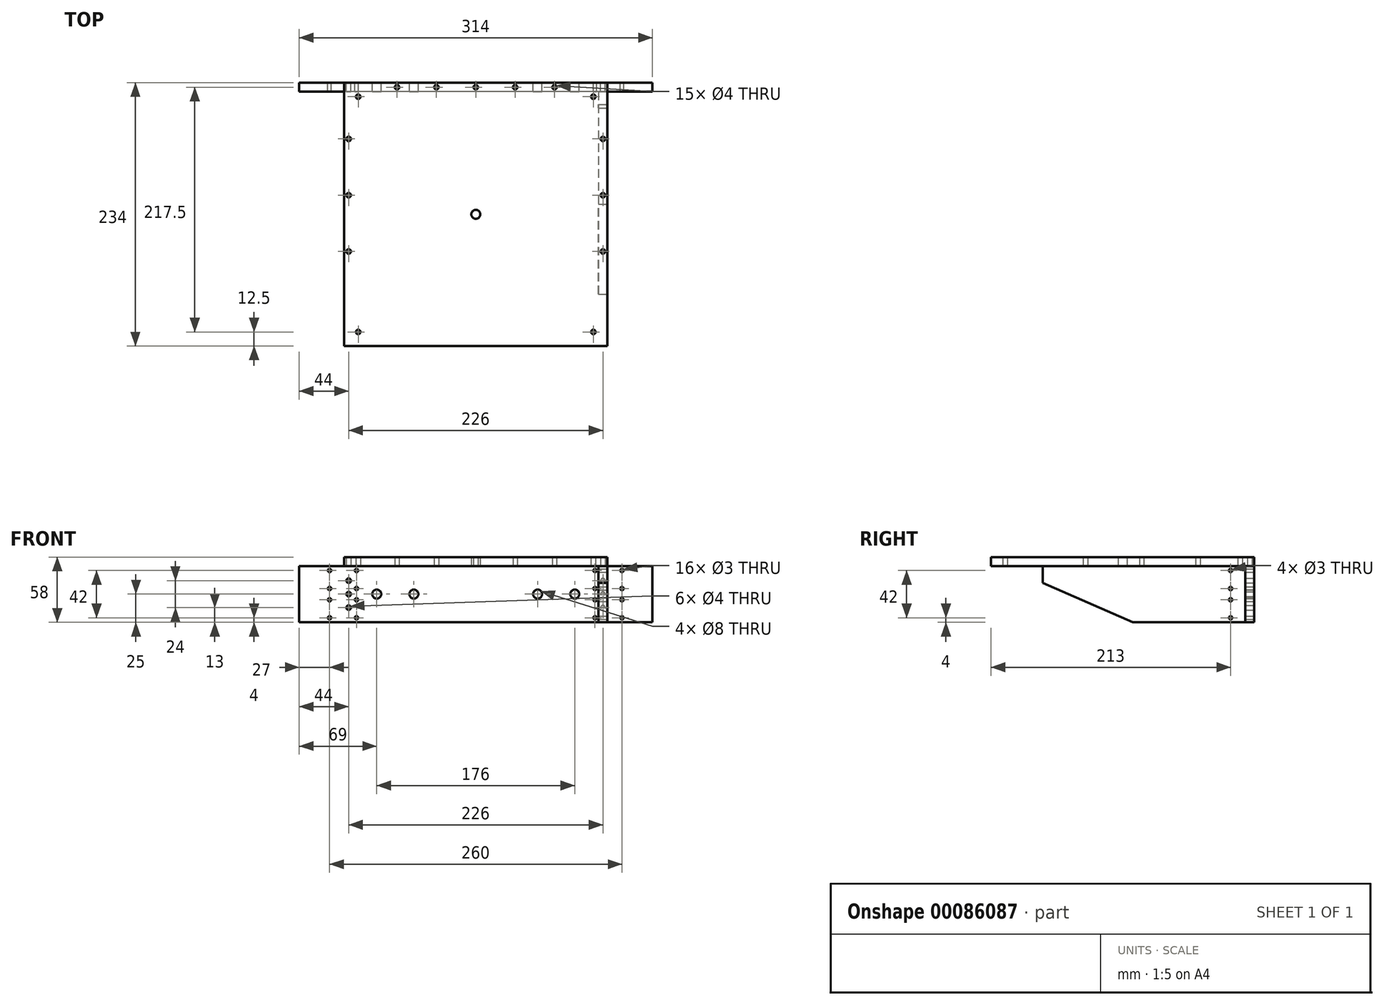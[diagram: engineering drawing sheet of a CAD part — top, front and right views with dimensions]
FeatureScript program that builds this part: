
annotation { "Feature Type Name" : "Feature", "Feature Type Description" : "" }
export const myFeature = defineFeature(function(context is Context, id is Id, definition is map)
    precondition{}
    {
        {
            var Q0;
            Q0=qCreatedBy(makeId("Top.planeOp"),FACE);
            var sketch = newSketch(context, id + "F0", { "sketchPlane" : qUnion([Q0])});
            skLineSegment(sketch, "E0.bottom", {"start": v(-117, 117) * mm, "end": v(117, 117) * mm});
            skLineSegment(sketch, "E0.top", {"start": v(-117, -117) * mm, "end": v(117, -117) * mm});
            skLineSegment(sketch, "E0.left", {"start": v(-117, 117) * mm, "end": v(-117, -117) * mm});
            skLineSegment(sketch, "E0.right", {"start": v(117, 117) * mm, "end": v(117, -117) * mm});
            skPoint(sketch, "E0.middle", {"position": v(0, 0) * mm});
            skLineSegment(sketch, "E1.bottom", {"start": v(104.5, 104.5) * mm, "end": v(-104.5, 104.5) * mm, "construction": true});
            skLineSegment(sketch, "E1.top", {"start": v(104.5, -104.5) * mm, "end": v(-104.5, -104.5) * mm, "construction": true});
            skLineSegment(sketch, "E1.left", {"start": v(104.5, 104.5) * mm, "end": v(104.5, -104.5) * mm, "construction": true});
            skLineSegment(sketch, "E1.right", {"start": v(-104.5, 104.5) * mm, "end": v(-104.5, -104.5) * mm, "construction": true});
            skPoint(sketch, "E2", {"position": v(-104.5, 104.5) * mm});
            skPoint(sketch, "E3", {"position": v(104.5, 104.5) * mm});
            skPoint(sketch, "E4", {"position": v(104.5, -104.5) * mm});
            skPoint(sketch, "E5", {"position": v(-104.5, -104.5) * mm});
            skLineSegment(sketch, "E6.bottom", {"start": v(-113, 113) * mm, "end": v(113, 113) * mm, "construction": true});
            skLineSegment(sketch, "E6.top", {"start": v(-113, -113) * mm, "end": v(113, -113) * mm, "construction": true});
            skLineSegment(sketch, "E6.left", {"start": v(-113, 113) * mm, "end": v(-113, -113) * mm, "construction": true});
            skLineSegment(sketch, "E6.right", {"start": v(113, 113) * mm, "end": v(113, -113) * mm, "construction": true});
            skPoint(sketch, "E7", {"position": v(113, 67) * mm});
            skPoint(sketch, "E8", {"position": v(113, 17) * mm});
            skPoint(sketch, "E9", {"position": v(113, -33) * mm});
            skPoint(sketch, "E10", {"position": v(113, -63) * mm});
            skPoint(sketch, "E11.MirrorP", {"position": v(-113, 67) * mm});
            skPoint(sketch, "E12.MirrorP", {"position": v(-113, 17) * mm});
            skPoint(sketch, "E13.MirrorP", {"position": v(-113, -33) * mm});
            skPoint(sketch, "E14.MirrorP", {"position": v(-113, -63) * mm});
            skPoint(sketch, "E15", {"position": v(0, 113) * mm});
            skPoint(sketch, "E16", {"position": v(35, 113) * mm});
            skPoint(sketch, "E17", {"position": v(70, 113) * mm});
            skPoint(sketch, "E18.MirrorP", {"position": v(-35, 113) * mm});
            skPoint(sketch, "E19.MirrorP", {"position": v(-70, 113) * mm});
            skSolve(sketch);
        }
        {
            var Q0;
            Q0=makeQuery(id+"F0.imprint","IMPRINT",FACE,{"disambiguationData":[TD([[makeQuery(id+"F0.imprint","IMPRINT",EDGE,{"derivedFrom":sQuery(id+"F0.wireOp",EDGE,"E0.bottom")}),-1.0]])]});
            extrude(context, id + "F1", {"entities" : qUnion([Q0]), "depth" : 8 * mm});
        }
        {
            var Q0;
            Q0=sQuery(id+"F0.wireOp",VERTEX,"E2");
            var Q1;
            Q1=sQuery(id+"F0.wireOp",VERTEX,"E3");
            var Q2;
            Q2=sQuery(id+"F0.wireOp",VERTEX,"E4");
            var Q3;
            Q3=sQuery(id+"F0.wireOp",VERTEX,"E5");
            var Q4;
            Q4=makeQuery(id+"F1.opExtrude","SWEPT_BODY",BODY,{"disambiguationData":[OSD([sQuery(id+"F0.wireOp",EDGE,"E0.bottom"),sQuery(id+"F0.wireOp",EDGE,"E0.top"),sQuery(id+"F0.wireOp",EDGE,"E0.left"),sQuery(id+"F0.wireOp",EDGE,"E0.right")])]});
            hole(context, id + "F2", {"style" : HoleStyle.SIMPLE, "endStyle" : HoleEndStyle.THROUGH, "oppositeDirection" : true, "holeDiameter" : 4 * mm, "locations" : qUnion([Q0, Q1, Q2, Q3]), "scope" : qUnion([Q4]), "isTappedThrough" : true});
        }
        {
            var Q0;
            Q0=sQuery(id+"F0.wireOp",VERTEX,"E0.middle");
            var Q1;
            Q1=makeQuery(id+"F1.opExtrude","SWEPT_BODY",BODY,{"disambiguationData":[OSD([sQuery(id+"F0.wireOp",EDGE,"E0.bottom"),sQuery(id+"F0.wireOp",EDGE,"E0.top"),sQuery(id+"F0.wireOp",EDGE,"E0.left"),sQuery(id+"F0.wireOp",EDGE,"E0.right")])]});
            hole(context, id + "F3", {"style" : HoleStyle.SIMPLE, "endStyle" : HoleEndStyle.THROUGH, "oppositeDirection" : true, "holeDiameter" : 8 * mm, "locations" : qUnion([Q0]), "scope" : qUnion([Q1]), "isTappedThrough" : true});
        }
        {
            var Q0;
            Q0=sQuery(id+"F0.wireOp",VERTEX,"E9");
            var Q1;
            Q1=sQuery(id+"F0.wireOp",VERTEX,"E8");
            var Q2;
            Q2=sQuery(id+"F0.wireOp",VERTEX,"E7");
            var Q3;
            Q3=sQuery(id+"F0.wireOp",VERTEX,"E17");
            var Q4;
            Q4=sQuery(id+"F0.wireOp",VERTEX,"E16");
            var Q5;
            Q5=sQuery(id+"F0.wireOp",VERTEX,"E15");
            var Q6;
            Q6=sQuery(id+"F0.wireOp",VERTEX,"E18.MirrorP");
            var Q7;
            Q7=sQuery(id+"F0.wireOp",VERTEX,"E19.MirrorP");
            var Q8;
            Q8=sQuery(id+"F0.wireOp",VERTEX,"E11.MirrorP");
            var Q9;
            Q9=sQuery(id+"F0.wireOp",VERTEX,"E12.MirrorP");
            var Q10;
            Q10=sQuery(id+"F0.wireOp",VERTEX,"E13.MirrorP");
            var Q11;
            Q11=makeQuery(id+"F1.opExtrude","SWEPT_BODY",BODY,{"disambiguationData":[OSD([sQuery(id+"F0.wireOp",EDGE,"E0.bottom"),sQuery(id+"F0.wireOp",EDGE,"E0.top"),sQuery(id+"F0.wireOp",EDGE,"E0.left"),sQuery(id+"F0.wireOp",EDGE,"E0.right")])]});
            hole(context, id + "F4", {"style" : HoleStyle.SIMPLE, "endStyle" : HoleEndStyle.THROUGH, "oppositeDirection" : true, "holeDiameter" : 4 * mm, "locations" : qUnion([Q0, Q1, Q2, Q3, Q4, Q5, Q6, Q7, Q8, Q9, Q10]), "scope" : qUnion([Q11]), "isTappedThrough" : true});
        }
        {
            var Q0;
            Q0=makeQuery(id+"F1.opExtrude","SWEPT_FACE",FACE,{"disambiguationData":[OSD([sQuery(id+"F0.wireOp",EDGE,"E0.bottom")])]});
            var sketch = newSketch(context, id + "F5", { "sketchPlane" : qUnion([Q0])});
            skLineSegment(sketch, "E20.bottom", {"start": v(-157, -50) * mm, "end": v(157, -50) * mm});
            skLineSegment(sketch, "E20.top", {"start": v(-157, 0) * mm, "end": v(157, 0) * mm});
            skLineSegment(sketch, "E20.left", {"start": v(-157, -50) * mm, "end": v(-157, 0) * mm});
            skLineSegment(sketch, "E20.right", {"start": v(157, -50) * mm, "end": v(157, 0) * mm});
            skPoint(sketch, "E20.middle", {"position": v(0, -25) * mm});
            skLineSegment(sketch, "E21", {"start": v(113, 0) * mm, "end": v(113, -50) * mm, "construction": true});
            skPoint(sketch, "E22", {"position": v(113, -25) * mm});
            skPoint(sketch, "E23", {"position": v(113, -13) * mm});
            skPoint(sketch, "E24", {"position": v(113, -37) * mm});
            skPoint(sketch, "E25.MirrorP", {"position": v(-113, -13) * mm});
            skPoint(sketch, "E26.MirrorP", {"position": v(-113, -25) * mm});
            skPoint(sketch, "E27.MirrorP", {"position": v(-113, -37) * mm});
            skLineSegment(sketch, "E28", {"start": v(-157, -25) * mm, "end": v(157, -25) * mm, "construction": true});
            skPoint(sketch, "E29", {"position": v(-55, -25) * mm});
            skPoint(sketch, "E30", {"position": v(-88, -25) * mm});
            skPoint(sketch, "E31.MirrorP", {"position": v(55, -25) * mm});
            skPoint(sketch, "E32.MirrorP", {"position": v(88, -25) * mm});
            skLineSegment(sketch, "E33", {"start": v(130, 0) * mm, "end": v(130, -50) * mm, "construction": true});
            skPoint(sketch, "E34", {"position": v(130, -4) * mm});
            skPoint(sketch, "E35", {"position": v(130, -20) * mm});
            skPoint(sketch, "E36.MirrorP", {"position": v(130, -30) * mm});
            skPoint(sketch, "E37.MirrorP", {"position": v(130, -46) * mm});
            skPoint(sketch, "E38.MirrorP", {"position": v(-130, -4) * mm});
            skPoint(sketch, "E39.MirrorP", {"position": v(-130, -20) * mm});
            skPoint(sketch, "E40.MirrorP", {"position": v(-130, -30) * mm});
            skPoint(sketch, "E41.MirrorP", {"position": v(-130, -46) * mm});
            skLineSegment(sketch, "E42", {"start": v(106, 0) * mm, "end": v(106, -50) * mm, "construction": true});
            skPoint(sketch, "E43", {"position": v(106, -4) * mm});
            skPoint(sketch, "E44", {"position": v(106, -20) * mm});
            skPoint(sketch, "E45", {"position": v(106, -30) * mm});
            skPoint(sketch, "E46", {"position": v(106, -46) * mm});
            skPoint(sketch, "E47.MirrorP", {"position": v(-106, -4) * mm});
            skPoint(sketch, "E48.MirrorP", {"position": v(-106, -20) * mm});
            skPoint(sketch, "E49.MirrorP", {"position": v(-106, -30) * mm});
            skPoint(sketch, "E50.MirrorP", {"position": v(-106, -46) * mm});
            skSolve(sketch);
        }
        {
            var Q0;
            Q0=makeQuery(id+"F5.imprint","IMPRINT",FACE,{"disambiguationData":[TD([[makeQuery(id+"F5.imprint","IMPRINT",EDGE,{"derivedFrom":sQuery(id+"F5.wireOp",EDGE,"E20.bottom")}),1.0]])]});
            extrude(context, id + "F6", {"entities" : qUnion([Q0]), "oppositeDirection" : true, "depth" : 8 * mm});
        }
        {
            var Q0;
            Q0=sQuery(id+"F5.wireOp",VERTEX,"E25.MirrorP");
            var Q1;
            Q1=sQuery(id+"F5.wireOp",VERTEX,"E26.MirrorP");
            var Q2;
            Q2=sQuery(id+"F5.wireOp",VERTEX,"E27.MirrorP");
            var Q3;
            Q3=sQuery(id+"F5.wireOp",VERTEX,"E24");
            var Q4;
            Q4=sQuery(id+"F5.wireOp",VERTEX,"E22");
            var Q5;
            Q5=sQuery(id+"F5.wireOp",VERTEX,"E23");
            var Q6;
            Q6=makeQuery(id+"F6.opExtrude","SWEPT_BODY",BODY,{"disambiguationData":[OSD([sQuery(id+"F5.wireOp",EDGE,"E20.bottom"),sQuery(id+"F5.wireOp",EDGE,"E20.top"),sQuery(id+"F5.wireOp",EDGE,"E20.left"),sQuery(id+"F5.wireOp",EDGE,"E20.right")])]});
            hole(context, id + "F7", {"style" : HoleStyle.SIMPLE, "endStyle" : HoleEndStyle.THROUGH, "holeDiameter" : 4 * mm, "locations" : qUnion([Q0, Q1, Q2, Q3, Q4, Q5]), "scope" : qUnion([Q6]), "isTappedThrough" : true});
        }
        {
            var Q0;
            Q0=sQuery(id+"F5.wireOp",VERTEX,"E29");
            var Q1;
            Q1=sQuery(id+"F5.wireOp",VERTEX,"E31.MirrorP");
            var Q2;
            Q2=makeQuery(id+"F6.opExtrude","SWEPT_BODY",BODY,{"disambiguationData":[OSD([sQuery(id+"F5.wireOp",EDGE,"E20.bottom"),sQuery(id+"F5.wireOp",EDGE,"E20.top"),sQuery(id+"F5.wireOp",EDGE,"E20.left"),sQuery(id+"F5.wireOp",EDGE,"E20.right")])]});
            hole(context, id + "F8", {"style" : HoleStyle.SIMPLE, "endStyle" : HoleEndStyle.THROUGH, "holeDiameter" : 8 * mm, "locations" : qUnion([Q0, Q1]), "scope" : qUnion([Q2]), "isTappedThrough" : true});
        }
        {
            var Q0;
            Q0=sQuery(id+"F5.wireOp",VERTEX,"E30");
            var Q1;
            Q1=sQuery(id+"F5.wireOp",VERTEX,"E32.MirrorP");
            var Q2;
            Q2=makeQuery(id+"F6.opExtrude","SWEPT_BODY",BODY,{"disambiguationData":[OSD([sQuery(id+"F5.wireOp",EDGE,"E20.bottom"),sQuery(id+"F5.wireOp",EDGE,"E20.top"),sQuery(id+"F5.wireOp",EDGE,"E20.left"),sQuery(id+"F5.wireOp",EDGE,"E20.right")])]});
            hole(context, id + "F9", {"style" : HoleStyle.SIMPLE, "endStyle" : HoleEndStyle.THROUGH, "holeDiameter" : 8 * mm, "locations" : qUnion([Q0, Q1]), "scope" : qUnion([Q2]), "isTappedThrough" : true});
        }
        {
            var Q0;
            Q0=sQuery(id+"F5.wireOp",VERTEX,"E38.MirrorP");
            var Q1;
            Q1=sQuery(id+"F5.wireOp",VERTEX,"E39.MirrorP");
            var Q2;
            Q2=sQuery(id+"F5.wireOp",VERTEX,"E40.MirrorP");
            var Q3;
            Q3=sQuery(id+"F5.wireOp",VERTEX,"E41.MirrorP");
            var Q4;
            Q4=sQuery(id+"F5.wireOp",VERTEX,"E47.MirrorP");
            var Q5;
            Q5=sQuery(id+"F5.wireOp",VERTEX,"E48.MirrorP");
            var Q6;
            Q6=sQuery(id+"F5.wireOp",VERTEX,"E49.MirrorP");
            var Q7;
            Q7=sQuery(id+"F5.wireOp",VERTEX,"E50.MirrorP");
            var Q8;
            Q8=sQuery(id+"F5.wireOp",VERTEX,"E43");
            var Q9;
            Q9=sQuery(id+"F5.wireOp",VERTEX,"E44");
            var Q10;
            Q10=sQuery(id+"F5.wireOp",VERTEX,"E45");
            var Q11;
            Q11=sQuery(id+"F5.wireOp",VERTEX,"E46");
            var Q12;
            Q12=sQuery(id+"F5.wireOp",VERTEX,"E37.MirrorP");
            var Q13;
            Q13=sQuery(id+"F5.wireOp",VERTEX,"E36.MirrorP");
            var Q14;
            Q14=sQuery(id+"F5.wireOp",VERTEX,"E35");
            var Q15;
            Q15=sQuery(id+"F5.wireOp",VERTEX,"E34");
            var Q16;
            Q16=makeQuery(id+"F6.opExtrude","SWEPT_BODY",BODY,{"disambiguationData":[OSD([sQuery(id+"F5.wireOp",EDGE,"E20.bottom"),sQuery(id+"F5.wireOp",EDGE,"E20.top"),sQuery(id+"F5.wireOp",EDGE,"E20.left"),sQuery(id+"F5.wireOp",EDGE,"E20.right")])]});
            hole(context, id + "F10", {"style" : HoleStyle.SIMPLE, "endStyle" : HoleEndStyle.THROUGH, "holeDiameter" : 3 * mm, "locations" : qUnion([Q0, Q1, Q2, Q3, Q4, Q5, Q6, Q7, Q8, Q9, Q10, Q11, Q12, Q13, Q14, Q15]), "scope" : qUnion([Q16]), "isTappedThrough" : true});
        }
        {
            var Q0;
            Q0=makeQuery(id+"F1.opExtrude","SWEPT_FACE",FACE,{"disambiguationData":[OSD([sQuery(id+"F0.wireOp",EDGE,"E0.right")])]});
            var sketch = newSketch(context, id + "F11", { "sketchPlane" : qUnion([Q0])});
            skLineSegment(sketch, "E51.bottom", {"start": v(109, -50) * mm, "end": v(-71, -50) * mm});
            skLineSegment(sketch, "E51.top", {"start": v(109, 0) * mm, "end": v(-71, 0) * mm});
            skLineSegment(sketch, "E51.left", {"start": v(109, -50) * mm, "end": v(109, 0) * mm});
            skLineSegment(sketch, "E51.right", {"start": v(-71, -50) * mm, "end": v(-71, 0) * mm});
            skPoint(sketch, "E52", {"position": v(-71, -15) * mm});
            skPoint(sketch, "E53", {"position": v(9, -50) * mm});
            skLineSegment(sketch, "E54", {"start": v(-71, -15) * mm, "end": v(9, -50) * mm});
            skLineSegment(sketch, "E55", {"start": v(96, 0) * mm, "end": v(96, -50) * mm, "construction": true});
            skPoint(sketch, "E56", {"position": v(96, -4) * mm});
            skPoint(sketch, "E57", {"position": v(96, -20) * mm});
            skLineSegment(sketch, "E58", {"start": v(109, -25) * mm, "end": v(-71, -25) * mm, "construction": true});
            skPoint(sketch, "E59.MirrorP", {"position": v(96, -46) * mm});
            skPoint(sketch, "E60.MirrorP", {"position": v(96, -30) * mm});
            skSolve(sketch);
        }
        {
            var Q0;
            {var subQ1=sQuery(id+"F11.wireOp",EDGE,"E51.top");Q0=makeQuery(id+"F11.imprint","IMPRINT",FACE,{"disambiguationData":[TD([[makeQuery(id+"F11.imprint","IMPRINT",EDGE,{"derivedFrom":subQ1}),1.0]])]});}
            extrude(context, id + "F12", {"entities" : qUnion([Q0]), "oppositeDirection" : true, "depth" : 8 * mm});
        }
        {
            var Q0;
            Q0=sQuery(id+"F11.wireOp",VERTEX,"E56");
            var Q1;
            Q1=sQuery(id+"F11.wireOp",VERTEX,"E57");
            var Q2;
            Q2=sQuery(id+"F11.wireOp",VERTEX,"E60.MirrorP");
            var Q3;
            Q3=sQuery(id+"F11.wireOp",VERTEX,"E59.MirrorP");
            var Q4;
            Q4=makeQuery(id+"F12.opExtrude","SWEPT_BODY",BODY,{"disambiguationData":[OSD([sQuery(id+"F11.wireOp",EDGE,"E51.bottom"),sQuery(id+"F11.wireOp",EDGE,"E51.top"),sQuery(id+"F11.wireOp",EDGE,"E51.left"),sQuery(id+"F11.wireOp",EDGE,"E51.right"),sQuery(id+"F11.wireOp",EDGE,"E54")])]});
            hole(context, id + "F13", {"style" : HoleStyle.SIMPLE, "endStyle" : HoleEndStyle.THROUGH, "holeDiameter" : 3 * mm, "locations" : qUnion([Q0, Q1, Q2, Q3]), "scope" : qUnion([Q4]), "isTappedThrough" : true});
        }
    });
